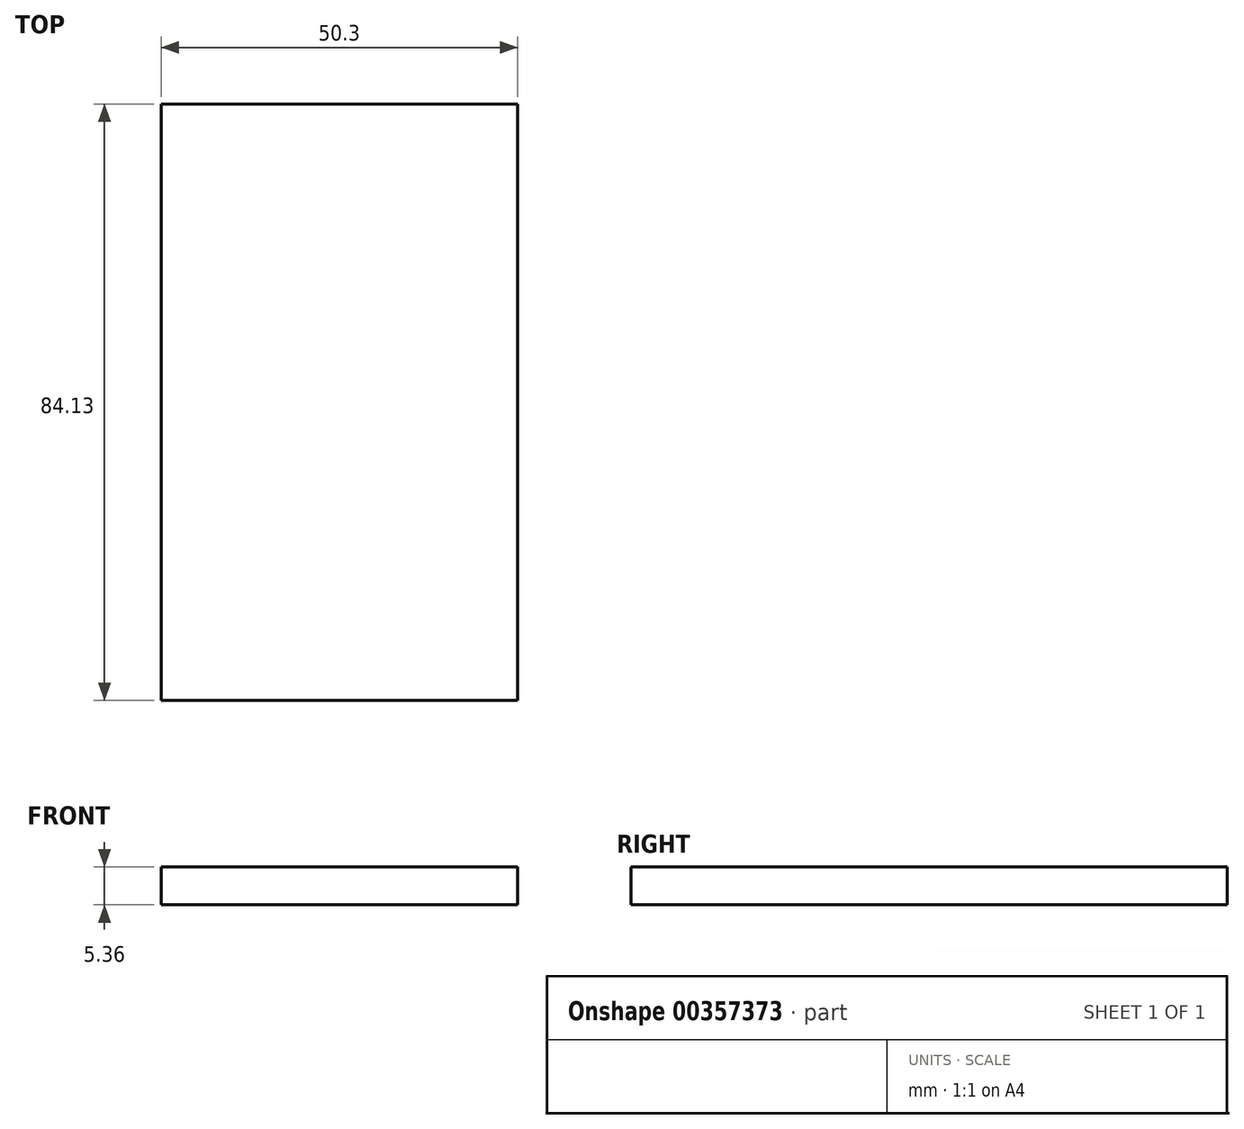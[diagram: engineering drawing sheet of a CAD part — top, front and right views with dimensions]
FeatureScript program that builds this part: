
annotation { "Feature Type Name" : "Feature", "Feature Type Description" : "" }
export const myFeature = defineFeature(function(context is Context, id is Id, definition is map)
    precondition{}
    {
        {
            var Q0;
            Q0=qCreatedBy(makeId("Right.planeOp"),FACE);
            var sketch = newSketch(context, id + "F0", { "sketchPlane" : qUnion([Q0])});
            skLineSegment(sketch, "E0", {"start": v(-47.54, 5.36) * mm, "end": v(36.59, 5.36) * mm});
            skLineSegment(sketch, "E1", {"start": v(36.59, 5.36) * mm, "end": v(36.59, 0) * mm});
            skLineSegment(sketch, "E2", {"start": v(36.59, 0) * mm, "end": v(-47.54, 0) * mm});
            skLineSegment(sketch, "E3", {"start": v(-47.54, 0) * mm, "end": v(-47.54, 5.36) * mm});
            skSolve(sketch);
        }
        {
            var Q0;
            Q0=makeQuery(id+"F0.imprint","IMPRINT",FACE,{"disambiguationData":[TD([[makeQuery(id+"F0.imprint","IMPRINT",EDGE,{"derivedFrom":sQuery(id+"F0.wireOp",EDGE,"E0")}),-1.0]])]});
            extrude(context, id + "F1", {"entities" : qUnion([Q0]), "endBound" : BoundingType.SYMMETRIC, "depth" : 50.3 * mm});
        }
    });
